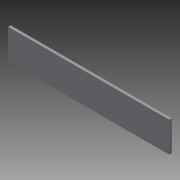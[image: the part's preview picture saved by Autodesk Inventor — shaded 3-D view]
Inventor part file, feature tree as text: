
AUTODESK INVENTOR PART (.ipt)
format: ipt  version: 2013 (Build 170138000, 138)  size: 68,608 bytes
history: native  units: in
note: dims shown in document units (in); Inventor stores cm internally (conversion verified against a paired STEP export)
features: other x3, sketch x1
ambient origin geometry x8: Origin, YZ Plane, XZ Plane, XY Plane, X Axis, Y Axis, Z Axis, Center Point
bodies: Solid1 (feature_tree)
feature tree (4):
  other  "FE-00036Base.ipt"
  other  "Solid1::FE-00036Base.ipt"
  other  "TaggingFeature1"
  sketch  "Sketch1"  dims[d0=0.3937in d1=3.0in d2=1.0in d3=0.25in d4=0.0in]
